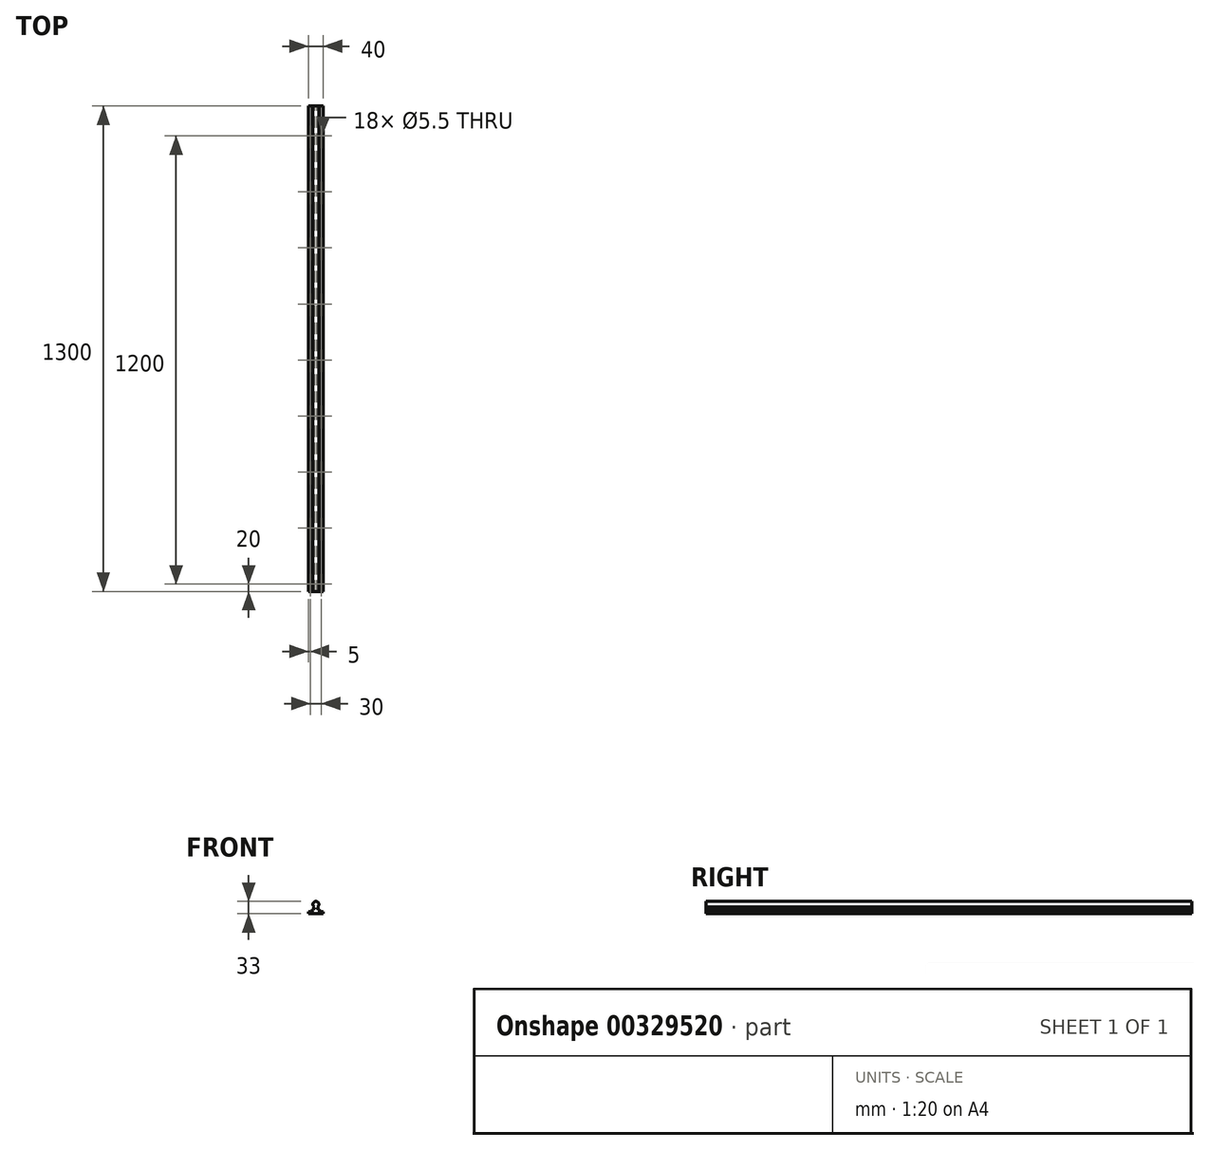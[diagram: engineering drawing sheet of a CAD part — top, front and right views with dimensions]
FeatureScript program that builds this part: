
annotation { "Feature Type Name" : "Feature", "Feature Type Description" : "" }
export const myFeature = defineFeature(function(context is Context, id is Id, definition is map)
    precondition{}
    {
        {
            var Q0;
            Q0=qCreatedBy(makeId("Front.planeOp"),FACE);
            var sketch = newSketch(context, id + "F0", { "sketchPlane" : qUnion([Q0])});
            skCircle(sketch, "E0", {"center": v(0, 0) * mm, "radius": 8 * mm});
            skLineSegment(sketch, "E1", {"start": v(-3.49, -7.2) * mm, "end": v(-7, -13.3) * mm});
            skLineSegment(sketch, "E2", {"start": v(-9.25, -13.3) * mm, "end": v(-9.25, -20) * mm});
            skLineSegment(sketch, "E3", {"start": v(-9.25, -20) * mm, "end": v(-20, -20) * mm});
            skLineSegment(sketch, "E4", {"start": v(-20, -20) * mm, "end": v(-20, -25) * mm});
            skLineSegment(sketch, "E5", {"start": v(-20, -25) * mm, "end": v(20, -25) * mm});
            skLineSegment(sketch, "E6", {"start": v(20, -25) * mm, "end": v(20, -20) * mm});
            skLineSegment(sketch, "E7", {"start": v(20, -20) * mm, "end": v(9.25, -20) * mm});
            skLineSegment(sketch, "E8", {"start": v(9.25, -20) * mm, "end": v(9.25, -13.3) * mm});
            skLineSegment(sketch, "E9", {"start": v(7, -13.3) * mm, "end": v(3.49, -7.2) * mm});
            skPoint(sketch, "E10", {"position": v(0, -25) * mm});
            skLineSegment(sketch, "E11", {"start": v(-9.25, -13.3) * mm, "end": v(-7, -13.3) * mm});
            skLineSegment(sketch, "E12", {"start": v(7, -13.3) * mm, "end": v(9.25, -13.3) * mm});
            skSolve(sketch);
        }
        {
            var Q0;
            Q0 = qSketchRegion(id + "F0", true);
            extrude(context, id + "F1", {"entities" : qUnion([Q0]), "endBound" : BoundingType.SYMMETRIC, "depth" : 1300 * mm});
        }
        {
            var Q0;
            Q0=makeQuery(id+"F1.opExtrude","SWEPT_FACE",FACE,{"disambiguationData":[OSD([sQuery(id+"F0.wireOp",EDGE,"E7")])]});
            var sketch = newSketch(context, id + "F2", { "sketchPlane" : qUnion([Q0])});
            skCircle(sketch, "E13", {"center": v(-15, -630) * mm, "radius": 2.75 * mm});
            skCircle(sketch, "E14", {"center": v(15, -630) * mm, "radius": 2.75 * mm});
            skCircle(sketch, "E15.0.1.0", {"center": v(-15, -480) * mm, "radius": 2.75 * mm});
            skCircle(sketch, "E15.0.1.1", {"center": v(15, -480) * mm, "radius": 2.75 * mm});
            skCircle(sketch, "E15.0.2.0", {"center": v(-15, -330) * mm, "radius": 2.75 * mm});
            skCircle(sketch, "E15.0.2.1", {"center": v(15, -330) * mm, "radius": 2.75 * mm});
            skCircle(sketch, "E15.0.3.0", {"center": v(-15, -180) * mm, "radius": 2.75 * mm});
            skCircle(sketch, "E15.0.3.1", {"center": v(15, -180) * mm, "radius": 2.75 * mm});
            skCircle(sketch, "E15.0.4.0", {"center": v(-15, -30) * mm, "radius": 2.75 * mm});
            skCircle(sketch, "E15.0.4.1", {"center": v(15, -30) * mm, "radius": 2.75 * mm});
            skCircle(sketch, "E15.0.5.0", {"center": v(-15, 120) * mm, "radius": 2.75 * mm});
            skCircle(sketch, "E15.0.5.1", {"center": v(15, 120) * mm, "radius": 2.75 * mm});
            skCircle(sketch, "E15.0.6.0", {"center": v(-15, 270) * mm, "radius": 2.75 * mm});
            skCircle(sketch, "E15.0.6.1", {"center": v(15, 270) * mm, "radius": 2.75 * mm});
            skCircle(sketch, "E15.0.7.0", {"center": v(-15, 420) * mm, "radius": 2.75 * mm});
            skCircle(sketch, "E15.0.7.1", {"center": v(15, 420) * mm, "radius": 2.75 * mm});
            skCircle(sketch, "E15.0.8.0", {"center": v(-15, 570) * mm, "radius": 2.75 * mm});
            skCircle(sketch, "E15.0.8.1", {"center": v(15, 570) * mm, "radius": 2.75 * mm});
            skLineSegment(sketch, "E15.direction1", {"start": v(-15, -630) * mm, "end": v(-40, -630) * mm, "construction": true});
            skLineSegment(sketch, "E15.direction2", {"start": v(-15, -630) * mm, "end": v(-15, -480) * mm, "construction": true});
            skSolve(sketch);
        }
        {
            var Q0;
            Q0 = qSketchRegion(id + "F2", true);
            extrude(context, id + "F3", {"entities" : qUnion([Q0]), "operationType" : NewBodyOperationType.REMOVE, "endBound" : BoundingType.THROUGH_ALL, "oppositeDirection" : true, "depth" : 25 * mm});
        }
    });
